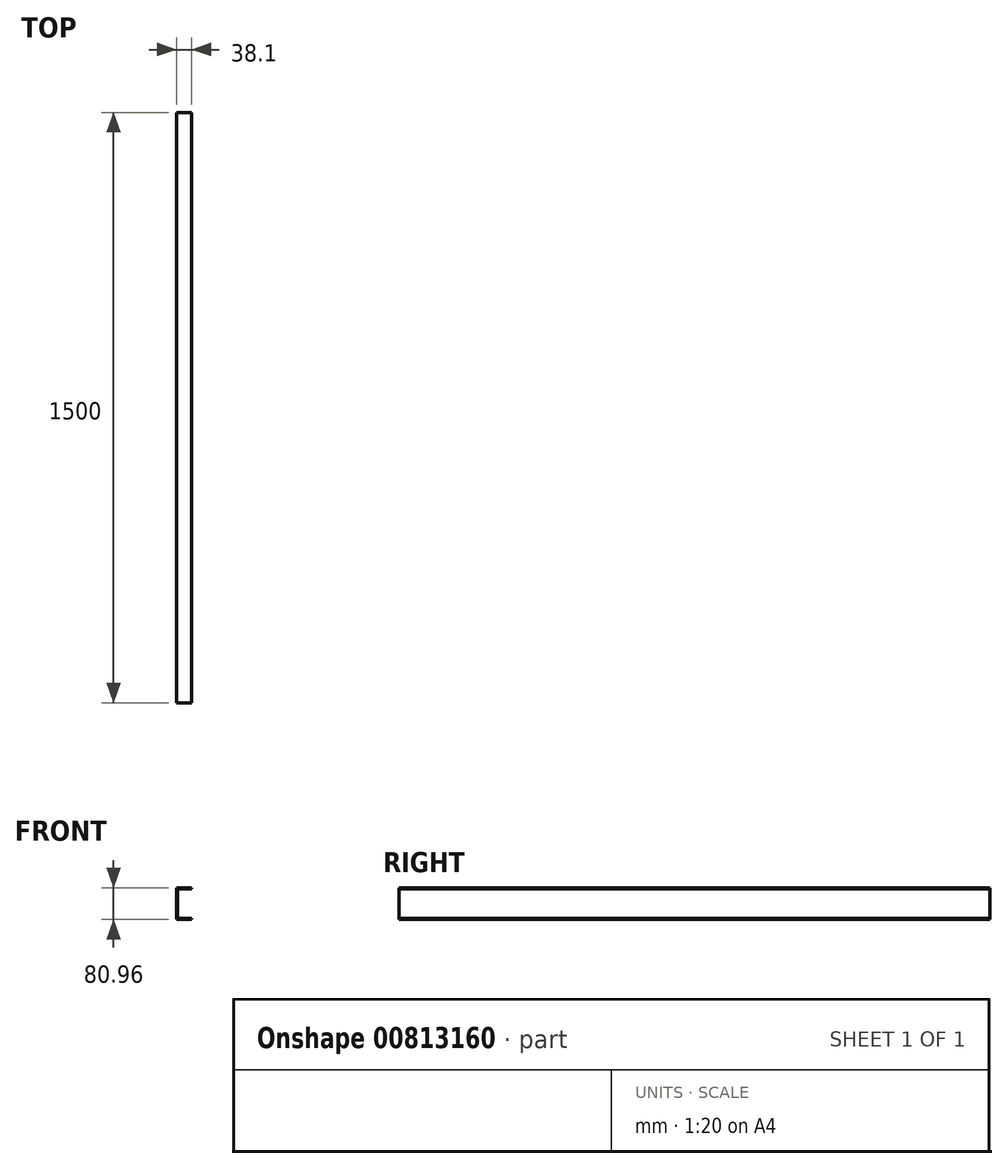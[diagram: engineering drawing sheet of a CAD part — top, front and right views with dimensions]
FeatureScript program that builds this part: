
annotation { "Feature Type Name" : "Feature", "Feature Type Description" : "" }
export const myFeature = defineFeature(function(context is Context, id is Id, definition is map)
    precondition{}
    {
        {
            var Q0;
            Q0=qCreatedBy(makeId("Front.planeOp"),FACE);
            var sketch = newSketch(context, id + "F0", { "sketchPlane" : qUnion([Q0])});
            skLineSegment(sketch, "E0", {"start": v(0, 0) * mm, "end": v(0, 80.96) * mm});
            skLineSegment(sketch, "E1", {"start": v(0, 80.96) * mm, "end": v(38.1, 80.96) * mm});
            skLineSegment(sketch, "E2", {"start": v(38.1, 80.96) * mm, "end": v(38.1, 77.79) * mm});
            skLineSegment(sketch, "E3", {"start": v(38.1, 77.79) * mm, "end": v(3.17, 77.79) * mm});
            skLineSegment(sketch, "E4", {"start": v(3.17, 77.79) * mm, "end": v(3.18, 3.17) * mm});
            skLineSegment(sketch, "E5", {"start": v(3.18, 3.17) * mm, "end": v(38.1, 3.18) * mm});
            skLineSegment(sketch, "E6", {"start": v(38.1, 3.18) * mm, "end": v(38.1, 0) * mm});
            skLineSegment(sketch, "E7", {"start": v(38.1, 0) * mm, "end": v(0, 0) * mm});
            skSolve(sketch);
        }
        {
            var Q0;
            Q0=qSketchRegion(id+"F0",true);
            extrude(context, id + "F1", {"entities" : qUnion([Q0]), "depth" : 1500 * mm, "offsetDistance" : 25.4 * mm});
        }
    });
